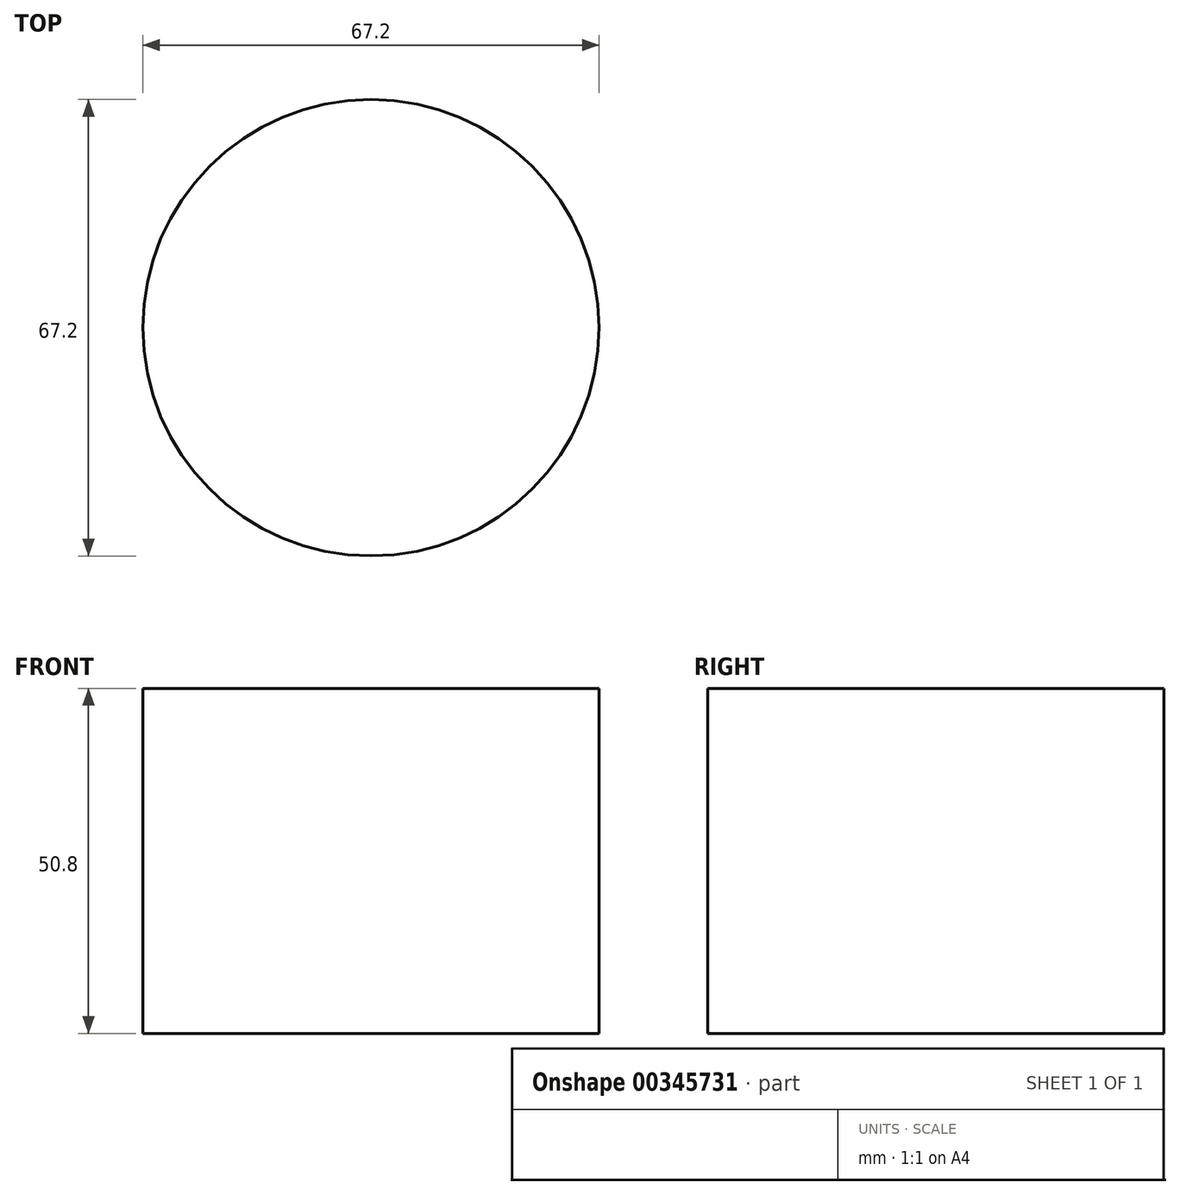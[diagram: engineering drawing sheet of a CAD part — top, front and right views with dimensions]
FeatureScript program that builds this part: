
annotation { "Feature Type Name" : "Feature", "Feature Type Description" : "" }
export const myFeature = defineFeature(function(context is Context, id is Id, definition is map)
    precondition{}
    {
        {
            var Q0;
            Q0=qCreatedBy(makeId("Top.planeOp"),FACE);
            var sketch = newSketch(context, id + "F0", { "sketchPlane" : qUnion([Q0])});
            skCircle(sketch, "E0", {"center": v(0, 0) * mm, "radius": 33.6 * mm});
            skSolve(sketch);
        }
        {
            var Q0;
            Q0=makeQuery(id+"F0.imprint","IMPRINT",FACE,{"disambiguationData":[TD([[makeQuery(id+"F0.imprint","IMPRINT",EDGE,{"derivedFrom":sQuery(id+"F0.wireOp",EDGE,"E0")}),1.0]])]});
            extrude(context, id + "F1", {"entities" : qUnion([Q0]), "depth" : 50.8 * mm});
        }
    });
